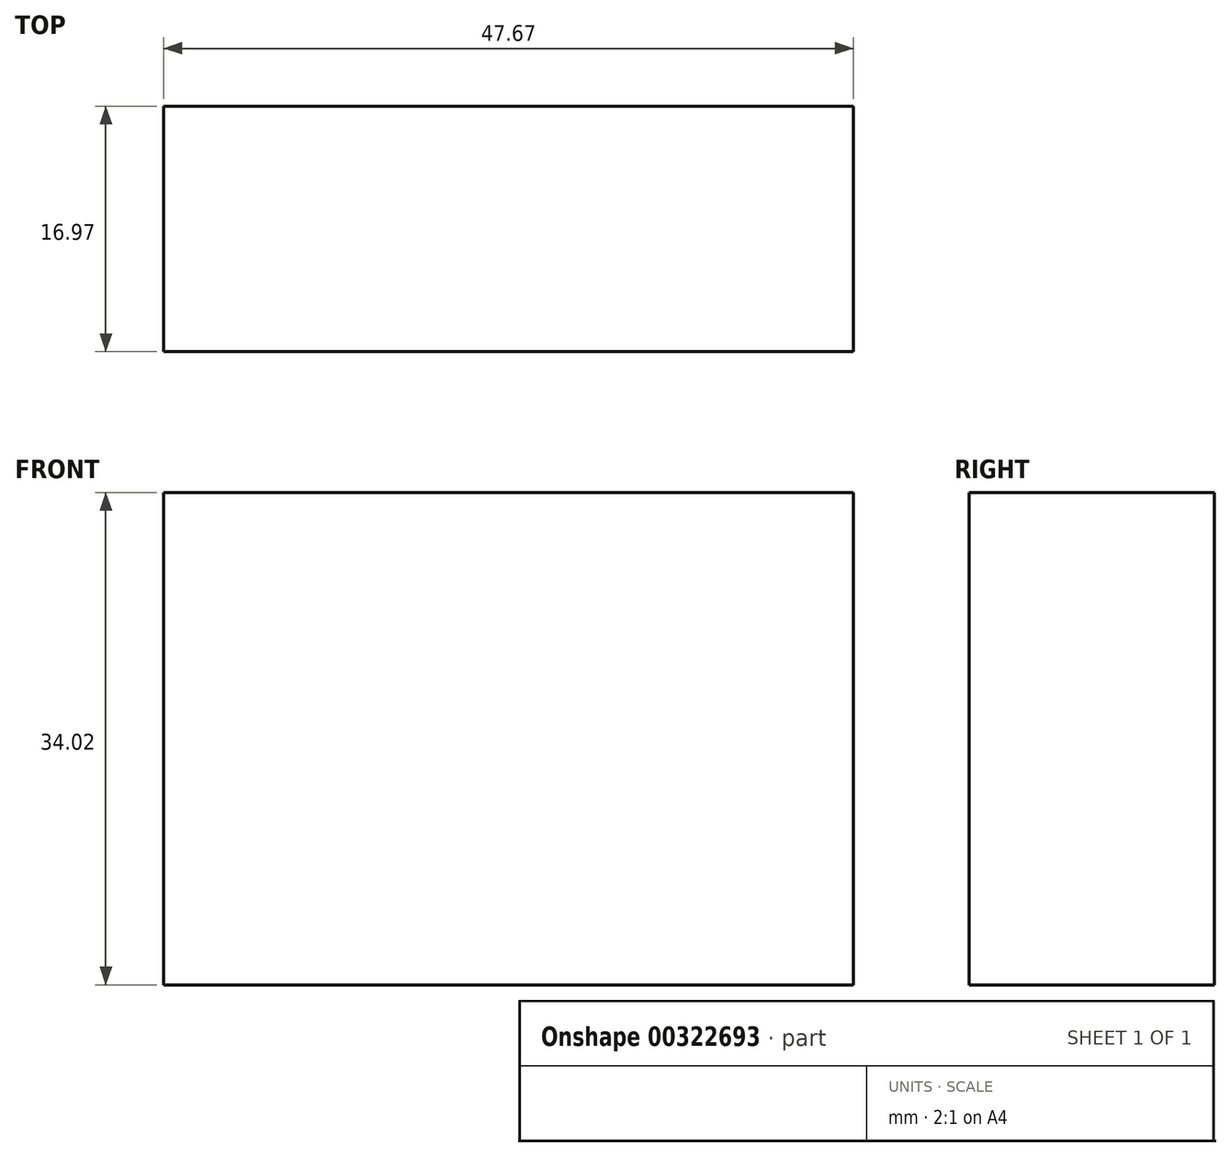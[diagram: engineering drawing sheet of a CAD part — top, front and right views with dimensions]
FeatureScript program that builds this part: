
annotation { "Feature Type Name" : "Feature", "Feature Type Description" : "" }
export const myFeature = defineFeature(function(context is Context, id is Id, definition is map)
    precondition{}
    {
        {
            var Q0;
            Q0=qCreatedBy(makeId("Front.planeOp"),FACE);
            var sketch = newSketch(context, id + "F0", { "sketchPlane" : qUnion([Q0])});
            skLineSegment(sketch, "E0.bottom", {"start": v(-47.67, 34.02) * mm, "end": v(0, 34.02) * mm});
            skLineSegment(sketch, "E0.top", {"start": v(-47.67, 0) * mm, "end": v(0, 0) * mm});
            skLineSegment(sketch, "E0.left", {"start": v(-47.67, 34.02) * mm, "end": v(-47.67, 0) * mm});
            skLineSegment(sketch, "E0.right", {"start": v(0, 34.02) * mm, "end": v(0, 0) * mm});
            skSolve(sketch);
        }
        {
            var Q0;
            Q0=makeQuery(id+"F0.imprint","IMPRINT",FACE,{"disambiguationData":[TD([[makeQuery(id+"F0.imprint","IMPRINT",EDGE,{"derivedFrom":sQuery(id+"F0.wireOp",EDGE,"E0.bottom")}),-1.0]])]});
            extrude(context, id + "F1", {"entities" : qUnion([Q0]), "depth" : 16.97 * mm});
        }
    });
